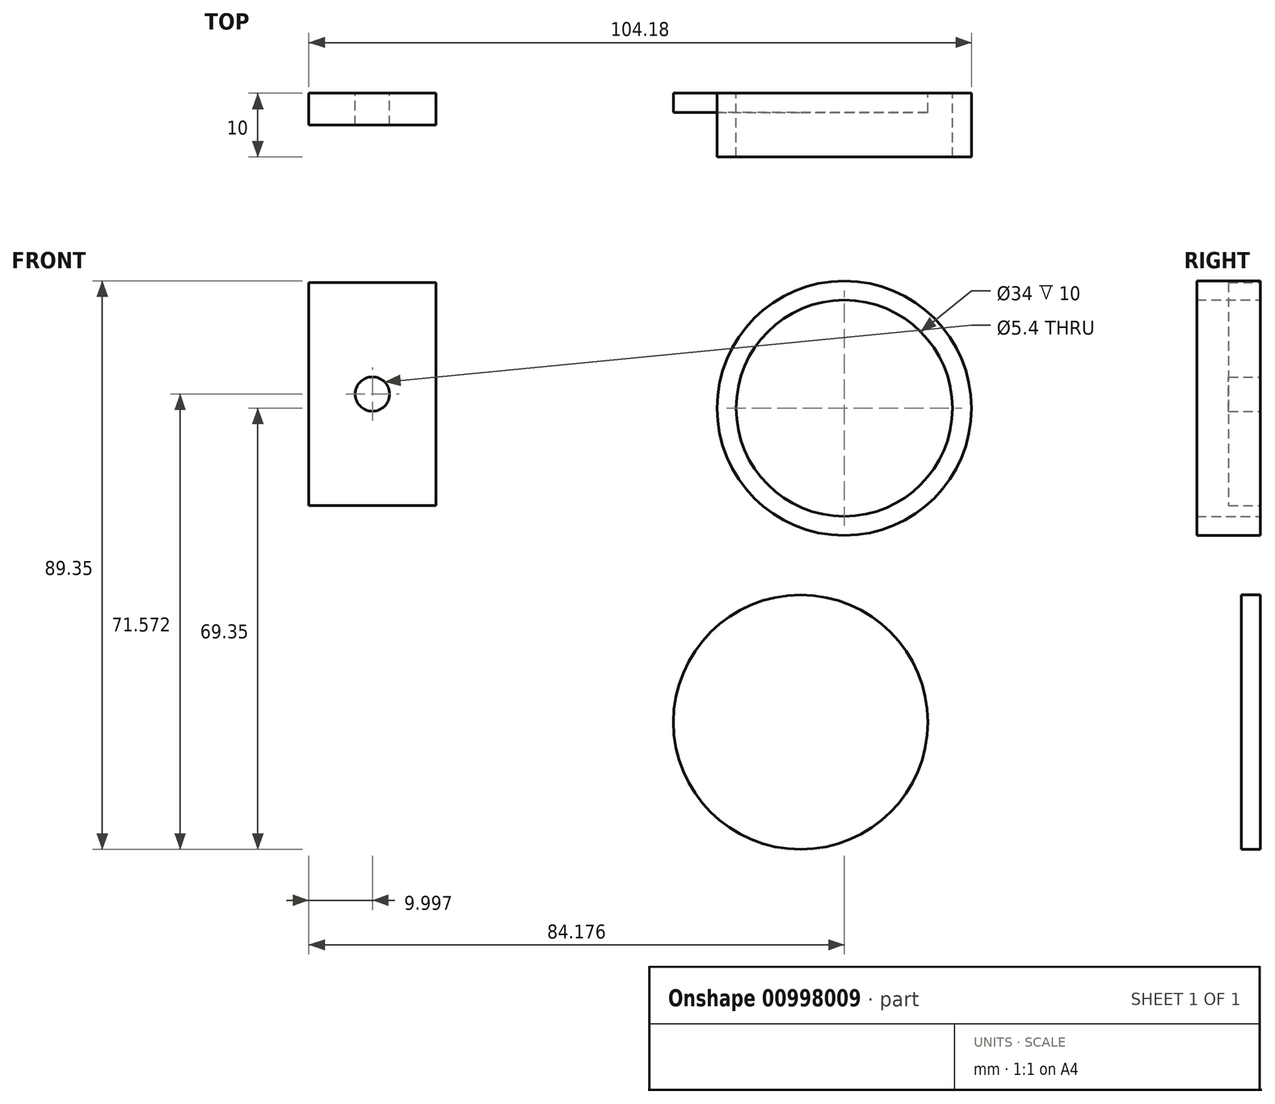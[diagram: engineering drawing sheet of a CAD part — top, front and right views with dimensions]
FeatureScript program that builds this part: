
annotation { "Feature Type Name" : "Feature", "Feature Type Description" : "" }
export const myFeature = defineFeature(function(context is Context, id is Id, definition is map)
    precondition{}
    {
        {
            var Q0;
            Q0=qCreatedBy(makeId("Front.planeOp"),FACE);
            var sketch = newSketch(context, id + "F0", { "sketchPlane" : qUnion([Q0])});
            skLineSegment(sketch, "E0.bottom", {"start": v(-61.03, 44.68) * mm, "end": v(-41.03, 44.68) * mm});
            skLineSegment(sketch, "E0.top", {"start": v(-61.03, 9.68) * mm, "end": v(-41.03, 9.68) * mm});
            skLineSegment(sketch, "E0.left", {"start": v(-61.03, 44.68) * mm, "end": v(-61.03, 9.68) * mm});
            skLineSegment(sketch, "E0.right", {"start": v(-41.03, 44.68) * mm, "end": v(-41.03, 9.68) * mm});
            skCircle(sketch, "E1", {"center": v(-51.03, 27.18) * mm, "radius": 2.7 * mm});
            skPoint(sketch, "E2", {"position": v(-51.03, 9.68) * mm});
            skPoint(sketch, "E3", {"position": v(-61.03, 27.18) * mm});
            skSolve(sketch);
        }
        {
            var Q0;
            Q0=makeQuery(id+"F0.imprint","IMPRINT",FACE,{"disambiguationData":[TD([[makeQuery(id+"F0.imprint","IMPRINT",EDGE,{"derivedFrom":sQuery(id+"F0.wireOp",EDGE,"E0.bottom")}),-1.0]])]});
            extrude(context, id + "F1", {"entities" : qUnion([Q0]), "depth" : 5 * mm, "offsetDistance" : 25 * mm});
        }
        {
            var Q0;
            Q0=qCreatedBy(makeId("Front.planeOp"),FACE);
            var sketch = newSketch(context, id + "F2", { "sketchPlane" : qUnion([Q0])});
            skCircle(sketch, "E4", {"center": v(23.15, 24.96) * mm, "radius": 20 * mm});
            skCircle(sketch, "E5", {"center": v(23.15, 24.96) * mm, "radius": 17 * mm});
            skSolve(sketch);
        }
        {
            var Q0;
            Q0 = qSketchRegion(id + "F2", true);
            extrude(context, id + "F3", {"entities" : qUnion([Q0]), "depth" : 10 * mm, "offsetDistance" : 25 * mm});
        }
        {
            var Q0;
            Q0=qCreatedBy(makeId("Front.planeOp"),FACE);
            var sketch = newSketch(context, id + "F4", { "sketchPlane" : qUnion([Q0])});
            skCircle(sketch, "E6", {"center": v(16.28, -24.39) * mm, "radius": 20 * mm});
            skSolve(sketch);
        }
        {
            var Q0;
            Q0 = qSketchRegion(id + "F4", true);
            extrude(context, id + "F5", {"entities" : qUnion([Q0]), "depth" : 3 * mm, "offsetDistance" : 25 * mm});
        }
    });
